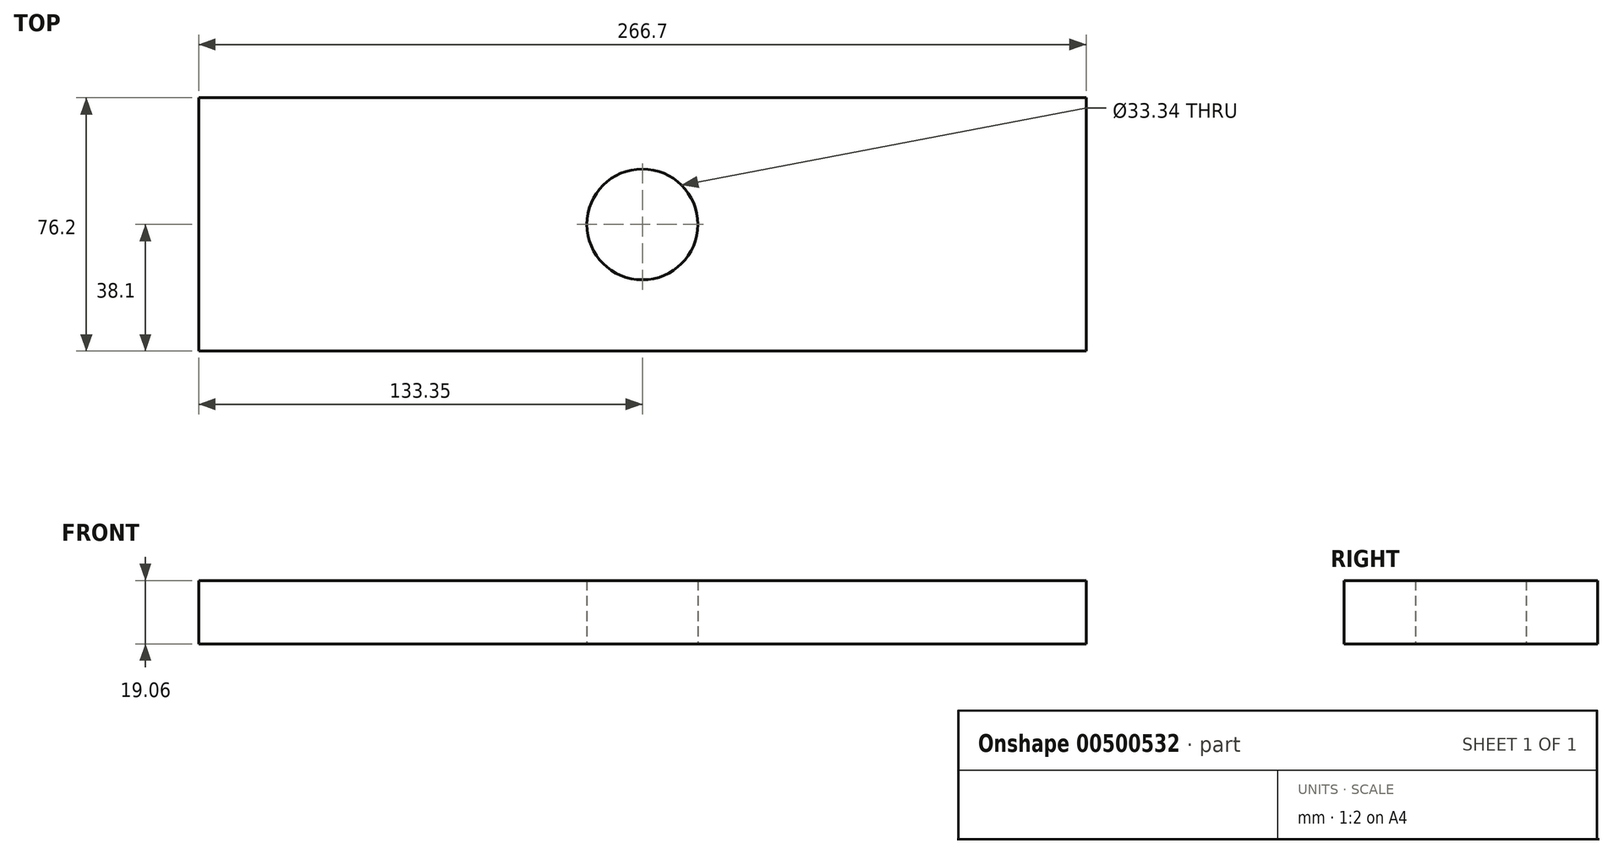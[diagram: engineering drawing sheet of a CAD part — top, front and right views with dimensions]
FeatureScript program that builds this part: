
annotation { "Feature Type Name" : "Feature", "Feature Type Description" : "" }
export const myFeature = defineFeature(function(context is Context, id is Id, definition is map)
    precondition{}
    {
        {
            var Q0;
            Q0=qCreatedBy(makeId("Top.planeOp"),FACE);
            var sketch = newSketch(context, id + "F0", { "sketchPlane" : qUnion([Q0])});
            skLineSegment(sketch, "E0.bottom", {"start": v(133.35, -38.1) * mm, "end": v(-133.35, -38.1) * mm});
            skLineSegment(sketch, "E0.top", {"start": v(133.35, 38.1) * mm, "end": v(-133.35, 38.1) * mm});
            skLineSegment(sketch, "E0.left", {"start": v(133.35, -38.1) * mm, "end": v(133.35, 38.1) * mm});
            skLineSegment(sketch, "E0.right", {"start": v(-133.35, -38.1) * mm, "end": v(-133.35, 38.1) * mm});
            skPoint(sketch, "E0.middle", {"position": v(0, 0) * mm});
            skCircle(sketch, "E1", {"center": v(0, 0) * mm, "radius": 16.67 * mm});
            skSolve(sketch);
        }
        {
            var Q0;
            Q0 = qSketchRegion(id + "F0", true);
            extrude(context, id + "F1", {"entities" : qUnion([Q0]), "endBound" : BoundingType.SYMMETRIC, "depth" : 19.05 * mm});
        }
    });
